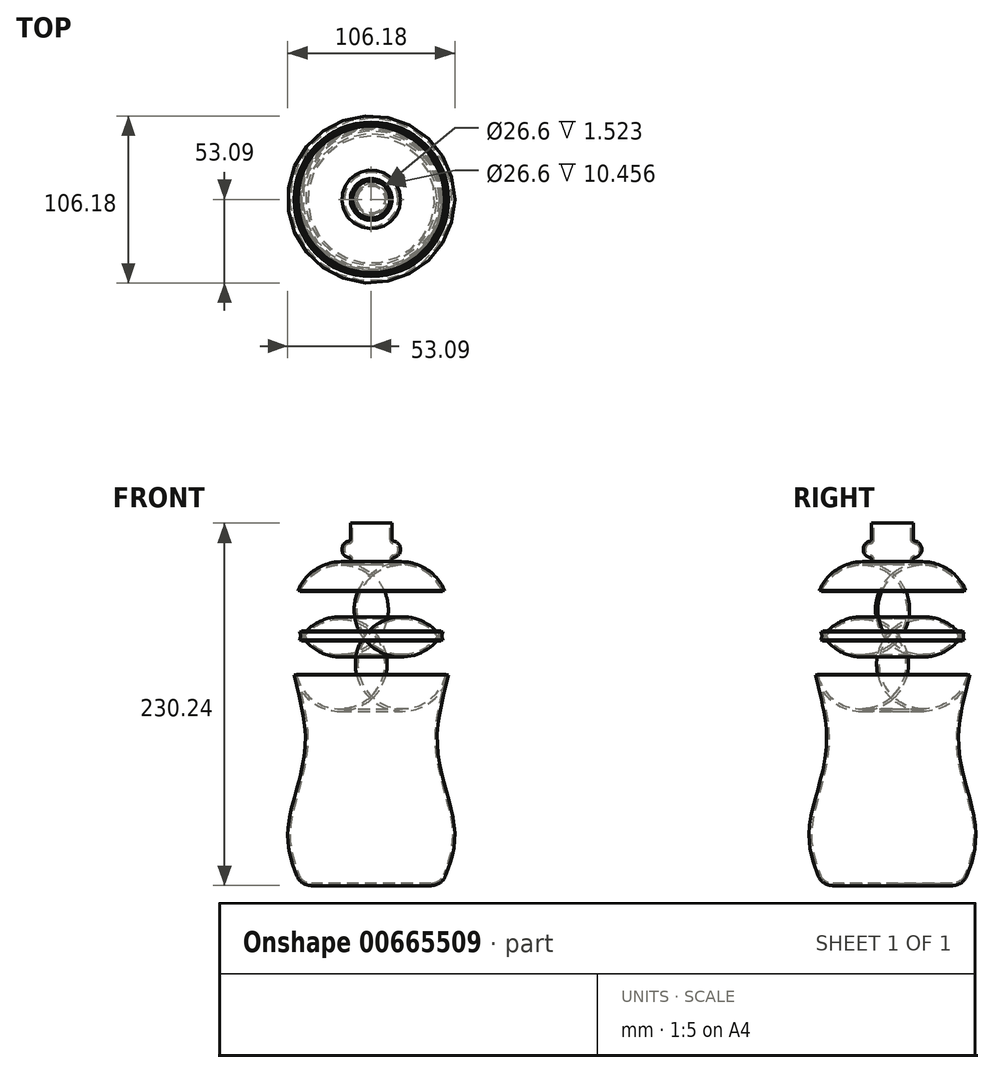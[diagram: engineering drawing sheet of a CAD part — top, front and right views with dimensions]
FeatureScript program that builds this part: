
annotation { "Feature Type Name" : "Feature", "Feature Type Description" : "" }
export const myFeature = defineFeature(function(context is Context, id is Id, definition is map)
    precondition{}
    {
        {
            var Q0;
            Q0=qCreatedBy(makeId("Right.planeOp"),FACE);
            var sketch = newSketch(context, id + "F0", { "sketchPlane" : qUnion([Q0])});
            skLineSegment(sketch, "E0", {"start": v(0, 80.92) * mm, "end": v(0, -124.85) * mm});
            skFitSpline(sketch, "E1", {"points": [v(36.52, 80.92) * mm, v(52.98, 34.82) * mm, v(41.84, -32.16) * mm, v(52.98, -89.43) * mm, v(44.75, -124.85) * mm], "startDerivative": vector(103.44, -166.36) * mm, "endDerivative": vector(-65.08, -159.2) * mm});
            skLineSegment(sketch, "E2", {"start": v(18.88, 80.92) * mm, "end": v(0, 80.92) * mm});
            skLineSegment(sketch, "E3", {"start": v(38, -124.85) * mm, "end": v(0, -124.85) * mm});
            skArc(sketch, "E4.filletArc", {"start": v(46.2, 63.34) * mm, "mid": v(35.12, 76.15) * mm, "end": v(18.88, 80.92) * mm});
            skArc(sketch, "E5.filletArc", {"start": v(38, -124.85) * mm, "mid": v(43.64, -123.1) * mm, "end": v(47.31, -118.47) * mm});
            skPoint(sketch, "E6.orphan", {"position": v(0, 97.51) * mm});
            skSolve(sketch);
        }
        {
            var Q0;
            Q0 = qSketchRegion(id + "F0", true);
            var Q1;
            Q1=sQuery(id+"F0.wireOp",EDGE,"E0");
            revolve(context, id + "F1", {"entities" : qUnion([Q0]), "axis" : qUnion([Q1]), "revolveType" : RevolveType.FULL});
        }
        {
            var Q0;
            Q0=qCreatedBy(makeId("Right.planeOp"),FACE);
            var sketch = newSketch(context, id + "F2", { "sketchPlane" : qUnion([Q0])});
            skLineSegment(sketch, "E7.bottom", {"start": v(0, 105.4) * mm, "end": v(13.3, 105.4) * mm});
            skLineSegment(sketch, "E7.top", {"start": v(0, 55.86) * mm, "end": v(13.3, 55.86) * mm});
            skLineSegment(sketch, "E7.left", {"start": v(0, 105.4) * mm, "end": v(0, 55.86) * mm});
            skLineSegment(sketch, "E7.right", {"start": v(13.3, 105.4) * mm, "end": v(13.3, 94.94) * mm});
            skArc(sketch, "E8", {"start": v(14.14, 83.43) * mm, "mid": v(18.62, 88.7) * mm, "end": v(14.14, 93.95) * mm});
            skLineSegment(sketch, "E9.trimOffspring", {"start": v(13.3, 82.45) * mm, "end": v(13.3, 55.86) * mm});
            skPoint(sketch, "E10.visualSharp", {"position": v(13.3, 94.02) * mm});
            skArc(sketch, "E10.filletArc", {"start": v(13.3, 94.94) * mm, "mid": v(13.54, 94.29) * mm, "end": v(14.14, 93.95) * mm});
            skPoint(sketch, "E11.visualSharp", {"position": v(13.3, 83.37) * mm});
            skArc(sketch, "E11.filletArc", {"start": v(14.14, 83.43) * mm, "mid": v(13.54, 83.1) * mm, "end": v(13.3, 82.45) * mm});
            skSolve(sketch);
        }
        {
            var Q0;
            Q0=makeQuery(id+"F2.imprint","IMPRINT",FACE,{"disambiguationData":[TD([[makeQuery(id+"F2.imprint","IMPRINT",EDGE,{"derivedFrom":sQuery(id+"F2.wireOp",EDGE,"E7.bottom")}),-1.0]])]});
            var Q1;
            Q1=sQuery(id+"F2.wireOp",EDGE,"E7.left");
            revolve(context, id + "F3", {"operationType" : NewBodyOperationType.ADD, "entities" : qUnion([Q0]), "axis" : qUnion([Q1]), "revolveType" : RevolveType.FULL});
        }
        {
            var Q0;
            Q0=qCreatedBy(makeId("Right.planeOp"),FACE);
            var sketch = newSketch(context, id + "F4", { "sketchPlane" : qUnion([Q0])});
            skLineSegment(sketch, "E12", {"start": v(65.34, 57.17) * mm, "end": v(46.34, 37.2) * mm});
            skLineSegment(sketch, "E13", {"start": v(46.52, 30.14) * mm, "end": v(69.09, 8.65) * mm});
            skLineSegment(sketch, "E14", {"start": v(69.09, 8.65) * mm, "end": v(65.34, 57.17) * mm});
            skPoint(sketch, "E15.visualSharp", {"position": v(42.9, 33.59) * mm});
            skArc(sketch, "E15.filletArc", {"start": v(46.34, 37.2) * mm, "mid": v(44.96, 33.64) * mm, "end": v(46.52, 30.14) * mm});
            skSolve(sketch);
        }
        {
            var Q0;
            Q0=makeQuery(id+"F4.imprint","IMPRINT",FACE,{"disambiguationData":[TD([[makeQuery(id+"F4.imprint","IMPRINT",EDGE,{"derivedFrom":sQuery(id+"F4.wireOp",EDGE,"E12")}),1.0]])]});
            var Q1;
            Q1=makeQuery(id+"F3.opRevolve","SWEPT_EDGE",EDGE,{"disambiguationData":[OSD([sQuery(id+"F2.wireOp",EDGE,"E7.bottom"),sQuery(id+"F2.wireOp",EDGE,"E7.right")])]});
            revolve(context, id + "F5", {"operationType" : NewBodyOperationType.REMOVE, "entities" : qUnion([Q0]), "axis" : qUnion([Q1]), "revolveType" : RevolveType.FULL, "oppositeDirection" : true});
        }
        {
            var Q0;
            Q0=makeQuery(id+"F5.boolean.opBoolean","INTERSECT",EDGE,{"derivedFrom":[makeQuery(id+"F1.opRevolve","SWEPT_FACE",FACE,{"disambiguationData":[OSD([sQuery(id+"F0.wireOp",EDGE,"E1")])]}),makeQuery(id+"F5.opRevolve","SWEPT_FACE",FACE,{"disambiguationData":[OSD([sQuery(id+"F4.wireOp",EDGE,"E12")])]})]});
            var Q1;
            Q1=makeQuery(id+"F5.boolean.opBoolean","INTERSECT",EDGE,{"derivedFrom":[makeQuery(id+"F1.opRevolve","SWEPT_FACE",FACE,{"disambiguationData":[OSD([sQuery(id+"F0.wireOp",EDGE,"E1")])]}),makeQuery(id+"F5.opRevolve","SWEPT_FACE",FACE,{"disambiguationData":[OSD([sQuery(id+"F4.wireOp",EDGE,"E13")])]})]});
            fillet(context, id + "F6", {"entities" : qUnion([Q0, Q1]), "radius" : 30 * mm, "tangentPropagation" : true, "allowEdgeOverflow" : false});
        }
        {
            var Q0;
            Q0=makeQuery(id+"F3.opRevolve","SWEPT_FACE",FACE,{"disambiguationData":[OSD([sQuery(id+"F2.wireOp",EDGE,"E7.bottom")])]});
            shell(context, id + "F7", {"entities" : qUnion([Q0]), "thickness" : 1.5 * mm});
        }
    });
